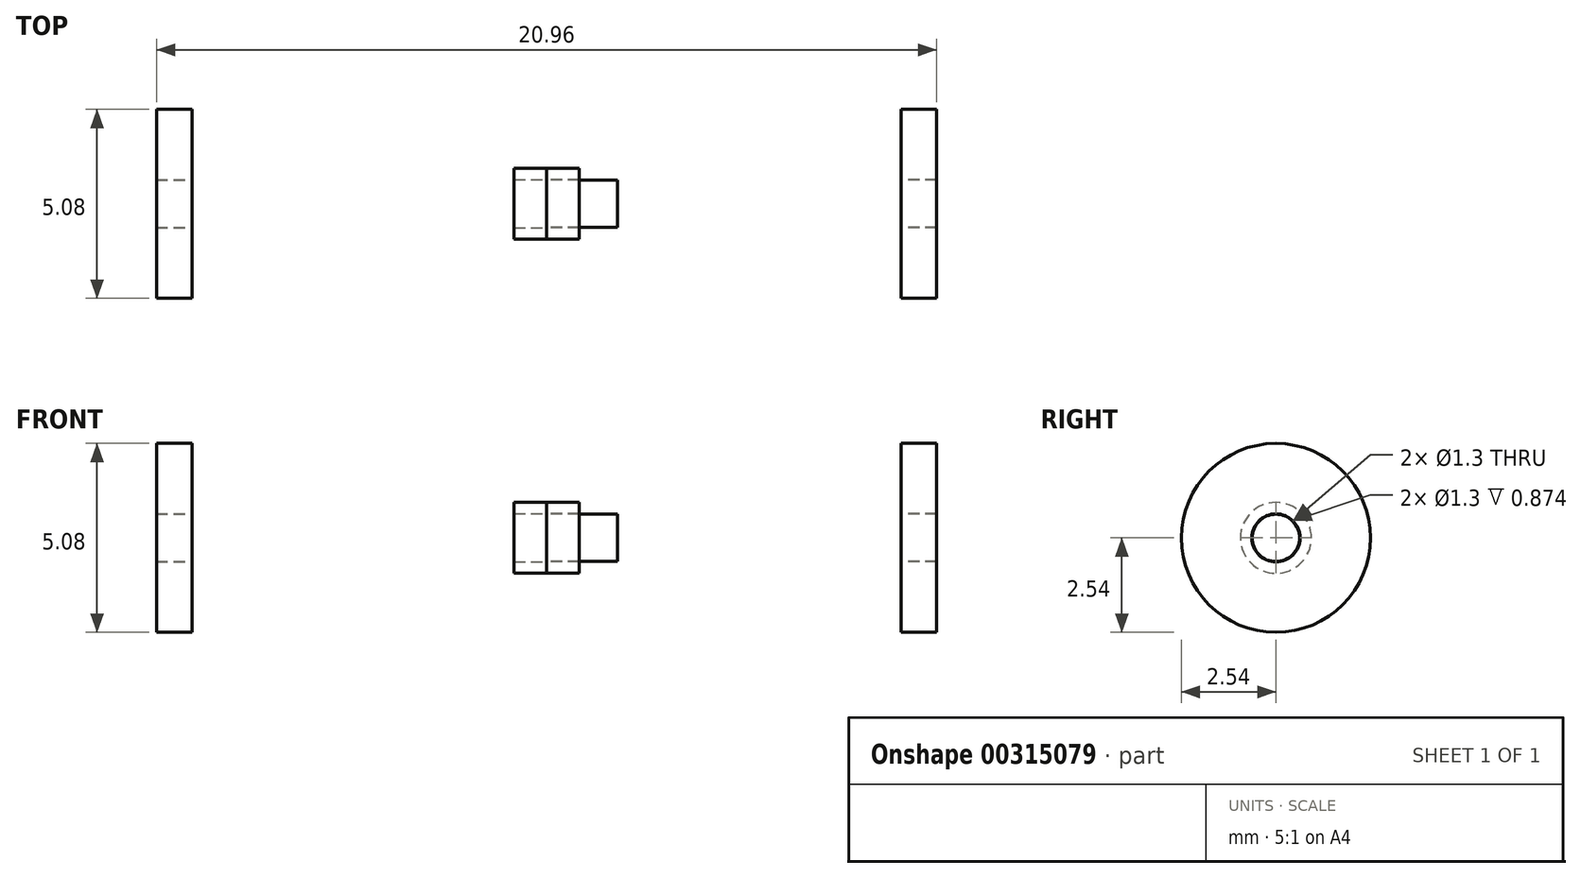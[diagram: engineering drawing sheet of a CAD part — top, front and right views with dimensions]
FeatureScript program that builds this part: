
annotation { "Feature Type Name" : "Feature", "Feature Type Description" : "" }
export const myFeature = defineFeature(function(context is Context, id is Id, definition is map)
    precondition{}
    {
        {
            var Q0;
            Q0=qCreatedBy(makeId("Right.planeOp"),FACE);
            var sketch = newSketch(context, id + "F0", { "sketchPlane" : qUnion([Q0])});
            skCircle(sketch, "E0", {"center": v(0, 0) * mm, "radius": 2.54 * mm});
            skCircle(sketch, "E1", {"center": v(0, 0) * mm, "radius": 0.64 * mm});
            skCircle(sketch, "E2", {"center": v(0, 0) * mm, "radius": 0.65 * mm});
            skCircle(sketch, "E3", {"center": v(0, 0) * mm, "radius": 0.95 * mm});
            skSolve(sketch);
        }
        {
            var Q0;
            Q0=makeQuery(id+"F0.imprint","IMPRINT",FACE,{"disambiguationData":[TD([[makeQuery(id+"F0.imprint","IMPRINT",EDGE,{"derivedFrom":sQuery(id+"F0.wireOp",EDGE,"E0")}),1.0]])]});
            extrude(context, id + "F1", {"entities" : qUnion([Q0]), "depth" : 0.95 * mm});
        }
        {
            var Q0;
            Q0=makeQuery(id+"F0.imprint","IMPRINT",FACE,{"disambiguationData":[TD([[makeQuery(id+"F0.imprint","IMPRINT",EDGE,{"derivedFrom":sQuery(id+"F0.wireOp",EDGE,"E1")}),1.0]])]});
            var Q1;
            Q1=makeQuery(id+"F0.imprint","IMPRINT",FACE,{"disambiguationData":[TD([[makeQuery(id+"F0.imprint","IMPRINT",EDGE,{"derivedFrom":sQuery(id+"F0.wireOp",EDGE,"E2")}),-1.0]])]});
            extrude(context, id + "F2", {"entities" : qUnion([Q0, Q1]), "operationType" : NewBodyOperationType.ADD, "depth" : 0.95 * mm});
        }
        {
            var Q0;
            Q0=makeQuery(id+"F1.opExtrude","SWEPT_BODY",BODY,{"disambiguationData":[OSD([sQuery(id+"F0.wireOp",EDGE,"E0"),sQuery(id+"F0.wireOp",EDGE,"E3")])]});
            var Q1;
            Q1=makeQuery(id+"F2.opExtrude","SWEPT_BODY",BODY,{"disambiguationData":[OSD([sQuery(id+"F0.wireOp",EDGE,"E1")])]});
            transform(context, id + "F3", {"entities" : qUnion([Q0, Q1]), "transformType" : TransformType.TRANSLATION_3D, "dx" : 9.52 * mm, "dy" : 0 * mm, "dz" : 0 * mm, "makeCopy" : false});
        }
        {
            var Q0;
            Q0=makeQuery(id+"F0.imprint","IMPRINT",FACE,{"disambiguationData":[TD([[makeQuery(id+"F0.imprint","IMPRINT",EDGE,{"derivedFrom":sQuery(id+"F0.wireOp",EDGE,"E1")}),1.0]])]});
            extrude(context, id + "F4", {"entities" : qUnion([Q0]), "operationType" : NewBodyOperationType.ADD, "depth" : 1.9 * mm});
        }
        {
            var Q0;
            Q0=makeQuery(id+"F0.imprint","IMPRINT",FACE,{"disambiguationData":[TD([[makeQuery(id+"F0.imprint","IMPRINT",EDGE,{"derivedFrom":sQuery(id+"F0.wireOp",EDGE,"E2")}),-1.0]])]});
            extrude(context, id + "F5", {"entities" : qUnion([Q0]), "depth" : 0.87 * mm});
        }
        {
            var Q0;
            Q0=makeQuery(id+"F1.opExtrude","SWEPT_BODY",BODY,{"disambiguationData":[OSD([sQuery(id+"F0.wireOp",EDGE,"E0"),sQuery(id+"F0.wireOp",EDGE,"E3")])]});
            var Q1;
            Q1=makeQuery(id+"F2.opExtrude","SWEPT_BODY",BODY,{"disambiguationData":[OSD([sQuery(id+"F0.wireOp",EDGE,"E1")])]});
            var Q2;
            Q2=makeQuery(id+"F5.opExtrude","SWEPT_BODY",BODY,{"disambiguationData":[OSD([sQuery(id+"F0.wireOp",EDGE,"E2"),sQuery(id+"F0.wireOp",EDGE,"E3")])]});
            var Q3;
            Q3=qCreatedBy(makeId("Right.planeOp"),FACE);
            mirror(context, id + "F6", {"entities" : qUnion([Q0, Q1, Q2]), "mirrorPlane" : qUnion([Q3])});
        }
    });
